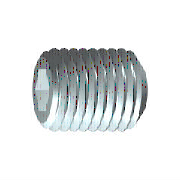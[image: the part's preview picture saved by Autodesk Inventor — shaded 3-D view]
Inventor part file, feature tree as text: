
AUTODESK INVENTOR PART (.ipt)
format: ipt  version: 2025.2 (Build 292293000, 293)  size: 176,128 bytes
history: native  units: mm (DEFAULTED — no unit token found)
features: extrude x1, other x1, plane x1
ambient origin geometry x8: Origin, YZ Plane, XZ Plane, XY Plane, X Axis, Y Axis, Z Axis, Center Point
bodies: Solid1 (feature_tree), Body (feature_tree)
feature tree (3):
  extrude  "Slot"  Depth=1.2mm
  other  "Work Axis1"
  plane  "Work Plane1"
